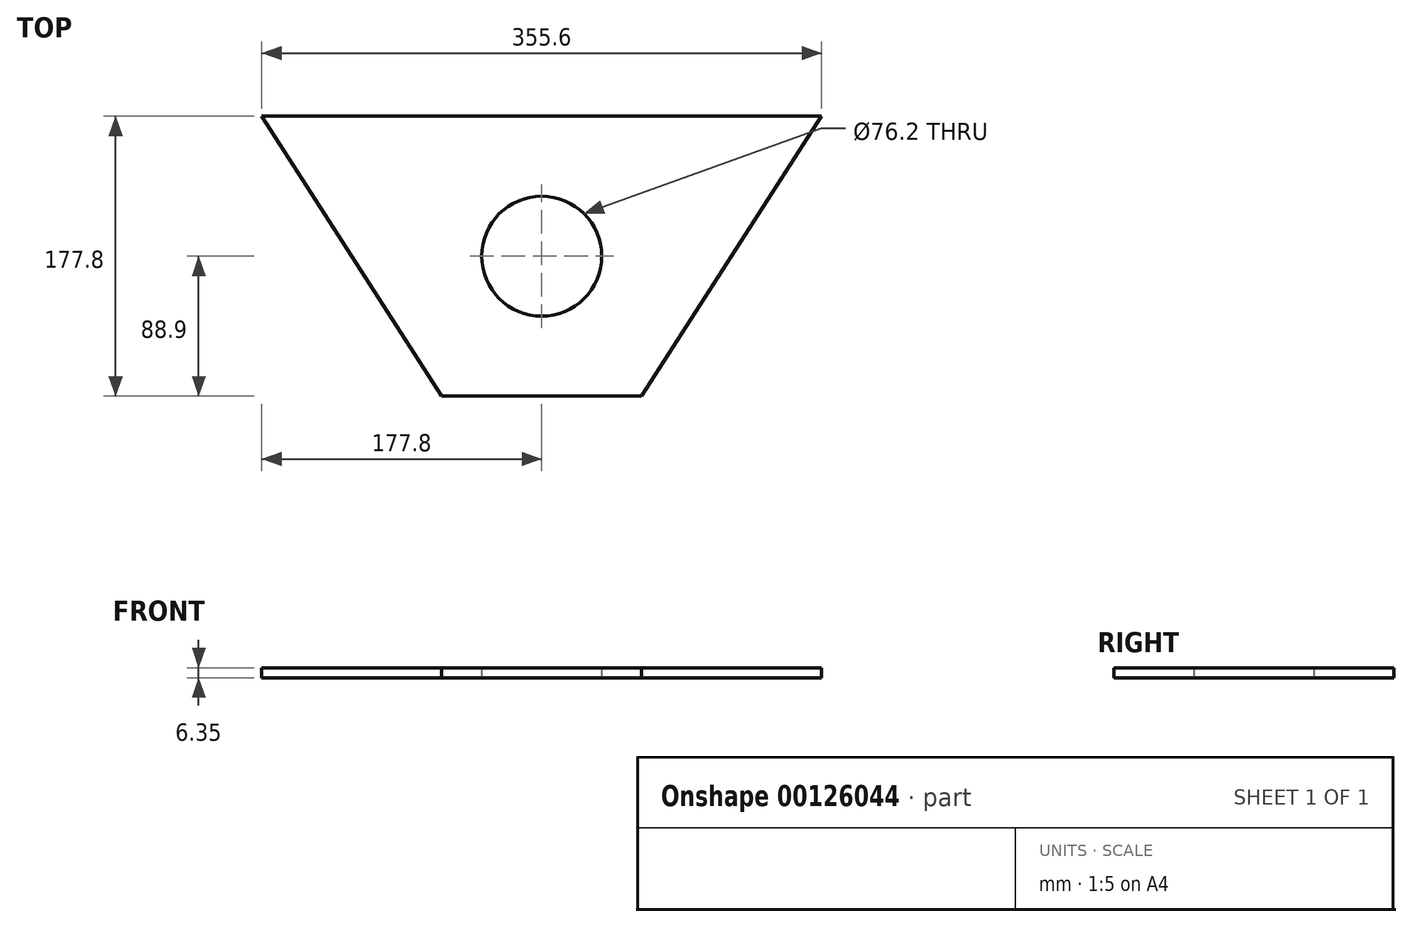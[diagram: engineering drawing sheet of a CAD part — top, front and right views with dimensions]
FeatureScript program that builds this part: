
annotation { "Feature Type Name" : "Feature", "Feature Type Description" : "" }
export const myFeature = defineFeature(function(context is Context, id is Id, definition is map)
    precondition{}
    {
        {
            var Q0;
            Q0=qCreatedBy(makeId("Top.planeOp"),FACE);
            var sketch = newSketch(context, id + "F0", { "sketchPlane" : qUnion([Q0])});
            skCircle(sketch, "E0", {"center": v(0, 0) * mm, "radius": 38.1 * mm});
            skLineSegment(sketch, "E1", {"start": v(0, 0) * mm, "end": v(0, -88.9) * mm});
            skLineSegment(sketch, "E2", {"start": v(0, -88.9) * mm, "end": v(63.5, -88.9) * mm});
            skLineSegment(sketch, "E3", {"start": v(63.5, -88.9) * mm, "end": v(63.5, -88.9) * mm});
            skLineSegment(sketch, "E4", {"start": v(177.8, 88.9) * mm, "end": v(63.5, -88.9) * mm});
            skLineSegment(sketch, "E5", {"start": v(177.8, 88.9) * mm, "end": v(0, 88.9) * mm});
            skLineSegment(sketch, "E6.MirrorCS", {"start": v(0, -88.9) * mm, "end": v(-63.5, -88.9) * mm});
            skLineSegment(sketch, "E7.MirrorCS", {"start": v(-177.8, 88.9) * mm, "end": v(-63.5, -88.9) * mm});
            skLineSegment(sketch, "E8.MirrorCS", {"start": v(-177.8, 88.9) * mm, "end": v(0, 88.9) * mm});
            skSolve(sketch);
        }
        {
            var Q0;
            Q0=makeQuery(id+"F0.imprint","IMPRINT",FACE,{"disambiguationData":[TD([[makeQuery(id+"F0.imprint","IMPRINT",EDGE,{"derivedFrom":sQuery(id+"F0.wireOp",EDGE,"E0")}),-1.0]])]});
            extrude(context, id + "F1", {"entities" : qUnion([Q0]), "depth" : 6.35 * mm});
        }
        {
            var Q0;
            Q0=makeQuery(id+"F1.opExtrude","SWEPT_BODY",BODY,{"disambiguationData":[OSD([sQuery(id+"F0.wireOp",EDGE,"E0"),sQuery(id+"F0.wireOp",EDGE,"E2"),sQuery(id+"F0.wireOp",EDGE,"E4"),sQuery(id+"F0.wireOp",EDGE,"E5"),sQuery(id+"F0.wireOp",EDGE,"E6.MirrorCS"),sQuery(id+"F0.wireOp",EDGE,"E7.MirrorCS"),sQuery(id+"F0.wireOp",EDGE,"E8.MirrorCS")])]});
            transform(context, id + "F2", {"entities" : qUnion([Q0]), "transformType" : TransformType.TRANSLATION_3D, "dx" : 0 * mm, "dy" : 0 * mm, "dz" : 0 * mm, "makeCopy" : true});
        }
        {
            var Q0;
            Q0=makeQuery(id+"F2.opPattern","COPY",BODY,{"derivedFrom":makeQuery(id+"F1.opExtrude","SWEPT_BODY",BODY,{"disambiguationData":[OSD([sQuery(id+"F0.wireOp",EDGE,"E0"),sQuery(id+"F0.wireOp",EDGE,"E2"),sQuery(id+"F0.wireOp",EDGE,"E4"),sQuery(id+"F0.wireOp",EDGE,"E5"),sQuery(id+"F0.wireOp",EDGE,"E6.MirrorCS"),sQuery(id+"F0.wireOp",EDGE,"E7.MirrorCS"),sQuery(id+"F0.wireOp",EDGE,"E8.MirrorCS")])]}),"instanceName":"1"});
            deleteBodies(context, id + "F3", {"entities" : qUnion([Q0])});
        }
    });
